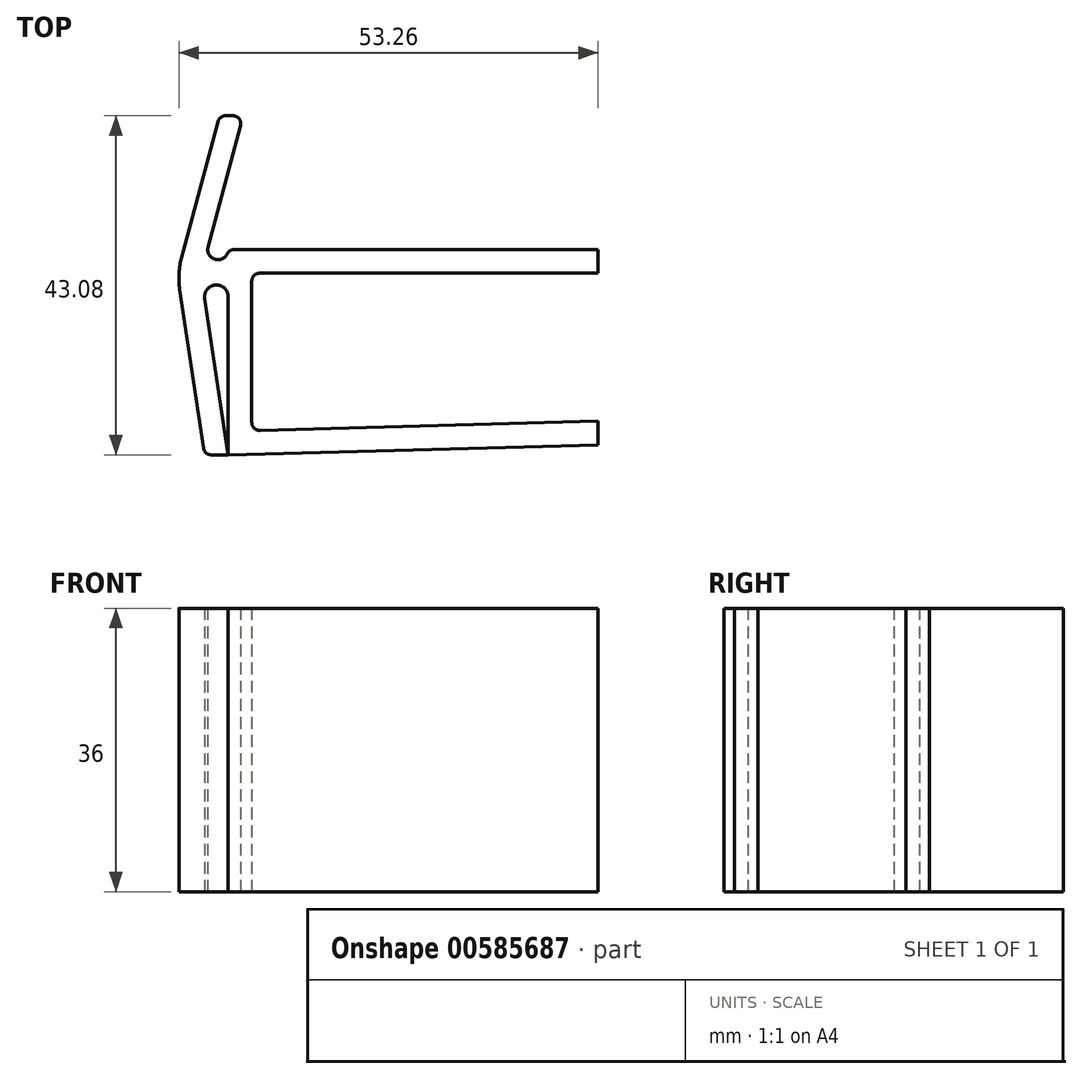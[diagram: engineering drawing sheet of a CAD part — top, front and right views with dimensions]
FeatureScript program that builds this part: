
annotation { "Feature Type Name" : "Feature", "Feature Type Description" : "" }
export const myFeature = defineFeature(function(context is Context, id is Id, definition is map)
    precondition{}
    {
        {
            var Q0;
            Q0=qCreatedBy(makeId("Top.planeOp"),FACE);
            var sketch = newSketch(context, id + "F0", { "sketchPlane" : qUnion([Q0])});
            skLineSegment(sketch, "E0", {"start": v(44, 0) * mm, "end": v(0, 0) * mm});
            skLineSegment(sketch, "E1", {"start": v(0, 0) * mm, "end": v(0, -20) * mm});
            skLineSegment(sketch, "E2", {"start": v(0, -20) * mm, "end": v(44, -18.8) * mm});
            skLineSegment(sketch, "E3", {"start": v(44, 0) * mm, "end": v(44, 3) * mm});
            skLineSegment(sketch, "E4", {"start": v(44, 3) * mm, "end": v(-3, 3) * mm});
            skLineSegment(sketch, "E5", {"start": v(-3, 3) * mm, "end": v(-3, -23.08) * mm});
            skLineSegment(sketch, "E6", {"start": v(-3, -23.08) * mm, "end": v(44, -21.8) * mm});
            skLineSegment(sketch, "E7", {"start": v(44, -21.8) * mm, "end": v(44, -18.8) * mm});
            skSolve(sketch);
        }
        {
            var Q0;
            Q0 = qSketchRegion(id + "F0", true);
            extrude(context, id + "F1", {"entities" : qUnion([Q0]), "depth" : 18 * mm, "offsetDistance" : 25 * mm, "hasSecondDirection" : true, "secondDirectionOppositeDirection" : true, "secondDirectionDepth" : 18 * mm});
        }
        {
            var Q0;
            Q0=qCreatedBy(makeId("Top.planeOp"),FACE);
            var sketch = newSketch(context, id + "F2", { "sketchPlane" : qUnion([Q0])});
            skLineSegment(sketch, "E8", {"start": v(-5.56, 3.34) * mm, "end": v(-1.1, 20) * mm});
            skLineSegment(sketch, "E9", {"start": v(-1.1, 20) * mm, "end": v(-4.1, 20) * mm});
            skLineSegment(sketch, "E10", {"start": v(-4.1, 20) * mm, "end": v(-9.45, 0) * mm});
            skLineSegment(sketch, "E11", {"start": v(-9.45, 0) * mm, "end": v(-6, -23.08) * mm});
            skLineSegment(sketch, "E12", {"start": v(-6, -23.08) * mm, "end": v(-3, -23.08) * mm});
            skLineSegment(sketch, "E13", {"start": v(-3, -23.08) * mm, "end": v(-5.97, -3.22) * mm});
            skArc(sketch, "E14", {"start": v(-3, -3) * mm, "mid": v(-4.6, -1.5) * mm, "end": v(-5.97, -3.22) * mm});
            skPoint(sketch, "E15.orphan", {"position": v(-3, 12.87) * mm});
            skArc(sketch, "E16", {"start": v(-5.56, 3.34) * mm, "mid": v(-4.47, 1.7) * mm, "end": v(-3, 3) * mm});
            skLineSegment(sketch, "E17", {"start": v(-3, 3) * mm, "end": v(-3, -3) * mm});
            skSolve(sketch);
        }
        {
            var Q0;
            Q0 = qSketchRegion(id + "F2", true);
            extrude(context, id + "F3", {"entities" : qUnion([Q0]), "operationType" : NewBodyOperationType.ADD, "depth" : 18 * mm, "offsetDistance" : 25 * mm, "hasSecondDirection" : true, "secondDirectionOppositeDirection" : true, "secondDirectionDepth" : 18 * mm});
        }
        {
            var Q0;
            Q0=makeQuery(id+"F3.opExtrude","SWEPT_EDGE",EDGE,{"disambiguationData":[OSD([sQuery(id+"F2.wireOp",EDGE,"E9"),sQuery(id+"F2.wireOp",EDGE,"E10")])]});
            var Q1;
            Q1=makeQuery(id+"F3.opExtrude","SWEPT_EDGE",EDGE,{"disambiguationData":[OSD([sQuery(id+"F2.wireOp",EDGE,"E8"),sQuery(id+"F2.wireOp",EDGE,"E9")])]});
            var Q2;
            Q2=makeQuery(id+"F3.boolean.opBoolean","MERGE",EDGE,{"derivedFrom":[makeQuery(id+"F1.opExtrude","SWEPT_EDGE",EDGE,{"disambiguationData":[OSD([sQuery(id+"F0.wireOp",EDGE,"E4"),sQuery(id+"F0.wireOp",EDGE,"E5")])]}),makeQuery(id+"F3.opExtrude","SWEPT_EDGE",EDGE,{"disambiguationData":[OSD([sQuery(id+"F2.wireOp",EDGE,"E16"),sQuery(id+"F2.wireOp",EDGE,"E17")])]})]});
            var Q3;
            Q3=makeQuery(id+"F3.opExtrude","SWEPT_EDGE",EDGE,{"disambiguationData":[OSD([sQuery(id+"F2.wireOp",EDGE,"E11"),sQuery(id+"F2.wireOp",EDGE,"E12")])]});
            fillet(context, id + "F4", {"entities" : qUnion([Q0, Q1, Q2, Q3]), "radius" : 1 * mm, "tangentPropagation" : true, "allowEdgeOverflow" : false});
        }
        {
            var Q0;
            Q0=makeQuery(id+"F3.opExtrude","SWEPT_EDGE",EDGE,{"disambiguationData":[OSD([sQuery(id+"F2.wireOp",EDGE,"E10"),sQuery(id+"F2.wireOp",EDGE,"E11")])]});
            fillet(context, id + "F5", {"entities" : qUnion([Q0]), "radius" : 10 * mm, "tangentPropagation" : true, "allowEdgeOverflow" : false});
        }
        {
            var Q0;
            Q0=makeQuery(id+"F1.opExtrude","SWEPT_EDGE",EDGE,{"disambiguationData":[OSD([sQuery(id+"F0.wireOp",EDGE,"E0"),sQuery(id+"F0.wireOp",EDGE,"E1")])]});
            var Q1;
            Q1=makeQuery(id+"F1.opExtrude","SWEPT_EDGE",EDGE,{"disambiguationData":[OSD([sQuery(id+"F0.wireOp",EDGE,"E1"),sQuery(id+"F0.wireOp",EDGE,"E2")])]});
            fillet(context, id + "F6", {"entities" : qUnion([Q0, Q1]), "radius" : 1 * mm, "tangentPropagation" : true, "allowEdgeOverflow" : false});
        }
    });
